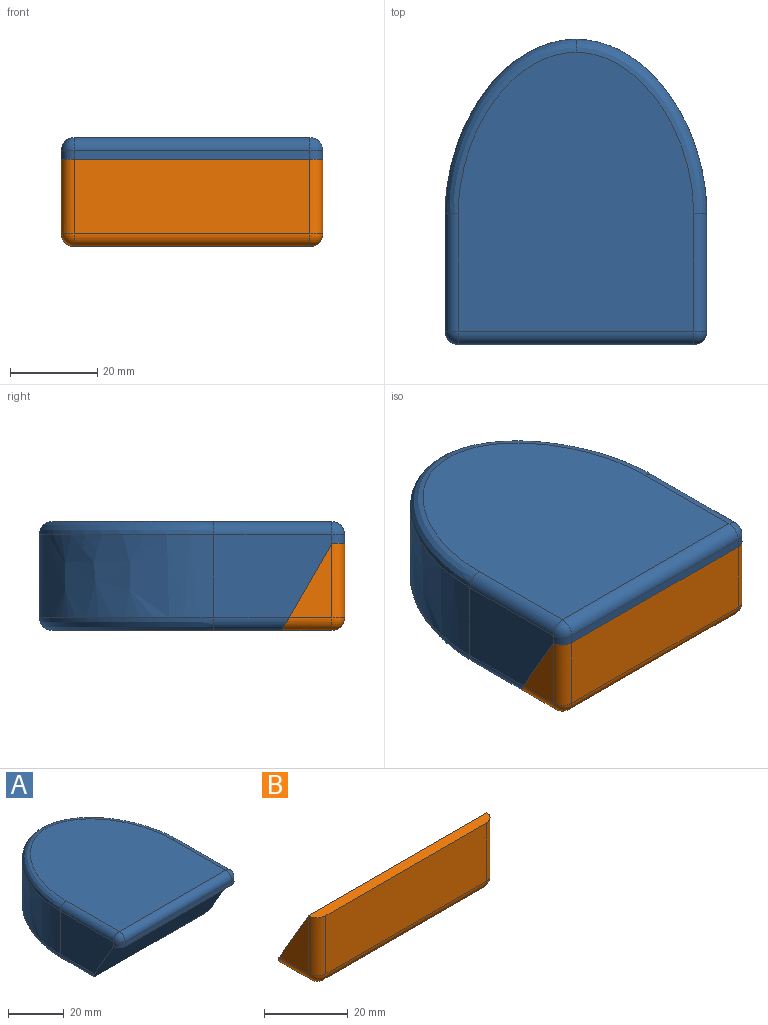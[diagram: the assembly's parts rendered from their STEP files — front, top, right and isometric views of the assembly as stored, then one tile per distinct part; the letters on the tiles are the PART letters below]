
ASSEMBLY  parts=2 mates=1
PART A: 35 faces, bbox 60.7x70.7x25.7 mm
  f0: plane 54x52.57mm, normal (0,0,-1), area 1361.1mm2, adj f7,f8,f9,f10,f15,f18,f19,f20
  f1: plane 27x19mm, normal (-1,0,0), area 431.5mm2, adj f5,f9,f13,f15,f34
  f2: plane 27x19mm, normal (1,0,0), area 431.5mm2, adj f4,f7,f11,f15,f30
  f3: plane 54x2mm, normal (0,-1,0), area 108mm2, adj f16,f30,f32,f34
  f4: extruded ~40x30mm, area 1043.5mm2, adj f2,f5,f8,f12
  f5: extruded ~40x30mm, area 1043.5mm2, adj f1,f4,f10,f14
  f6: plane 64x54mm, normal (0,0,1), area 3002.6mm2, adj f11,f12,f13,f14,f32
  f7: cylinder r=3mm len=17.3mm, axis (0,1,0), area 77.4mm2, adj f0,f2,f8,f15
  f8: bspline ~52.56x33.41mm, area 250.7mm2, adj f0,f4,f7,f10
  f9: cylinder r=3mm len=17.3mm, axis (0,-1,0), area 77.4mm2, adj f0,f1,f10,f15
  f10: bspline ~52.56x42.56mm, area 250.7mm2, adj f0,f5,f8,f9
  f11: cylinder r=3mm len=27mm, axis (0,-1,0), area 127.2mm2, adj f2,f6,f12,f31
  f12: bspline ~52.56x42.56mm, area 250.7mm2, adj f4,f6,f11,f14
  f13: cylinder r=3mm len=27mm, axis (0,1,0), area 127.2mm2, adj f1,f6,f14,f33
  f14: bspline ~52.56x33.41mm, area 250.7mm2, adj f5,f6,f12,f13
  f15: plane 60.73x20.73mm, normal (0,-0.87,-0.5), area 1381.2mm2, adj f0,f1,f2,f7,f9,f16,f30,f34
  f16: plane 60x2.89mm, normal (0,0,-1), area 169.3mm2, adj f3,f15,f30,f34
  f17: plane 44x3mm, normal (0,1,0), area 132mm2, adj f18,f21,f22,f29
  f18: plane 10x6mm, normal (1,0,0), area 45mm2, adj f0,f17,f19,f22,f28,f29
  f19: extruded ~32x22mm, area 159mm2, adj f0,f18,f20,f22,f26,f27
  f20: extruded ~32x22mm, area 159mm2, adj f0,f19,f21,f22,f23,f27
  f21: plane 10x6mm, normal (-1,0,0), area 45mm2, adj f0,f17,f20,f22,f28,f29
  f22: plane 44x42mm, normal (0,0,-1), area 1521.8mm2, adj f17,f18,f19,f20,f21
  f23: plane 5.21x3mm, normal (0,-1,0), area 15.6mm2, adj f0,f20,f24,f27
  f24: extruded ~16.49x15.34mm, area 71.5mm2, adj f0,f23,f25,f27
  f25: extruded ~16.49x15.34mm, area 71.5mm2, adj f0,f24,f26,f27
  f26: plane 5.21x3mm, normal (0,-1,0), area 15.6mm2, adj f0,f19,f25,f27
  f27: plane 41.16x21.51mm, normal (0,0,1), area 277.7mm2, adj f19,f20,f23,f24,f25,f26
  f28: plane 44x3mm, normal (0,1,0), area 132mm2, adj f0,f18,f21,f29
  f29: plane 44x5mm, normal (0,0,1), area 220mm2, adj f17,f18,f21,f28
  f30: cylinder r=3mm len=3mm, axis (0,0,1), area 9.4mm2, adj f2,f3,f15,f16,f31
  f31: sphere r=3mm, area 14.1mm2, adj f11,f30,f32
  f32: cylinder r=3mm len=54mm, axis (-1,0,0), area 254.5mm2, adj f3,f6,f31,f33
  f33: sphere r=3mm, area 14.1mm2, adj f13,f32,f34
  f34: cylinder r=3mm len=3mm, axis (0,0,-1), area 9.4mm2, adj f1,f3,f15,f16,f33
PART B: 13 faces, bbox 60x14.4x20 mm
  f0: plane 16.8x9.7mm, normal (1,0,0), area 81.5mm2, adj f5,f6,f7
  f1: plane 16.8x9.7mm, normal (-1,0,0), area 81.5mm2, adj f5,f8,f9
  f2: plane 54x11.43mm, normal (0,0,-1), area 617.4mm2, adj f5,f7,f8,f12
  f3: plane 54x17mm, normal (0,-1,0), area 918mm2, adj f4,f6,f9,f12
  f4: plane 60x2.89mm, normal (0,0,1), area 169.3mm2, adj f3,f5,f6,f9
  f5: plane 60x20mm, normal (0,0.87,0.5), area 1381.2mm2, adj f0,f1,f2,f4,f6,f7,f8,f9
  f6: cylinder r=3mm len=17mm, axis (0,0,1), area 80.1mm2, adj f0,f3,f4,f5,f10
  f7: cylinder r=3mm len=11.43mm, axis (0,-1,0), area 50.9mm2, adj f0,f2,f5,f10
  f8: cylinder r=3mm len=11.43mm, axis (0,1,0), area 50.9mm2, adj f1,f2,f5,f11
  f9: cylinder r=3mm len=17mm, axis (0,0,-1), area 80.1mm2, adj f1,f3,f4,f5,f11
  f10: sphere r=3mm, area 14.1mm2, adj f6,f7,f12
  f11: sphere r=3mm, area 14.1mm2, adj f8,f9,f12
  f12: cylinder r=3mm len=54mm, axis (-1,0,0), area 254.5mm2, adj f2,f3,f10,f11
PLACE A t=(0,15.57,0)mm
PLACE B at identity
MATE fastened A.f15 <-> B.f5  axis (0,-0.87,-0.5) through (0,0,-12.5)mm
